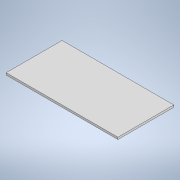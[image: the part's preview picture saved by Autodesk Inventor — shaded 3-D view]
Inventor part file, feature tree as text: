
AUTODESK INVENTOR PART (.ipt)
format: ipt  version: 2020 (Build 240168000, 168)  size: 92,160 bytes
history: native  units: mm
features: extrude x1, sketch x1
ambient origin geometry x8: Origin, YZ Plane, XZ Plane, XY Plane, X Axis, Y Axis, Z Axis, Center Point
bodies: Solide1 (feature_tree)
feature tree (2):
  extrude  "Extrusion1"  Depth=320.0mm
  sketch  "Esquisse1"
